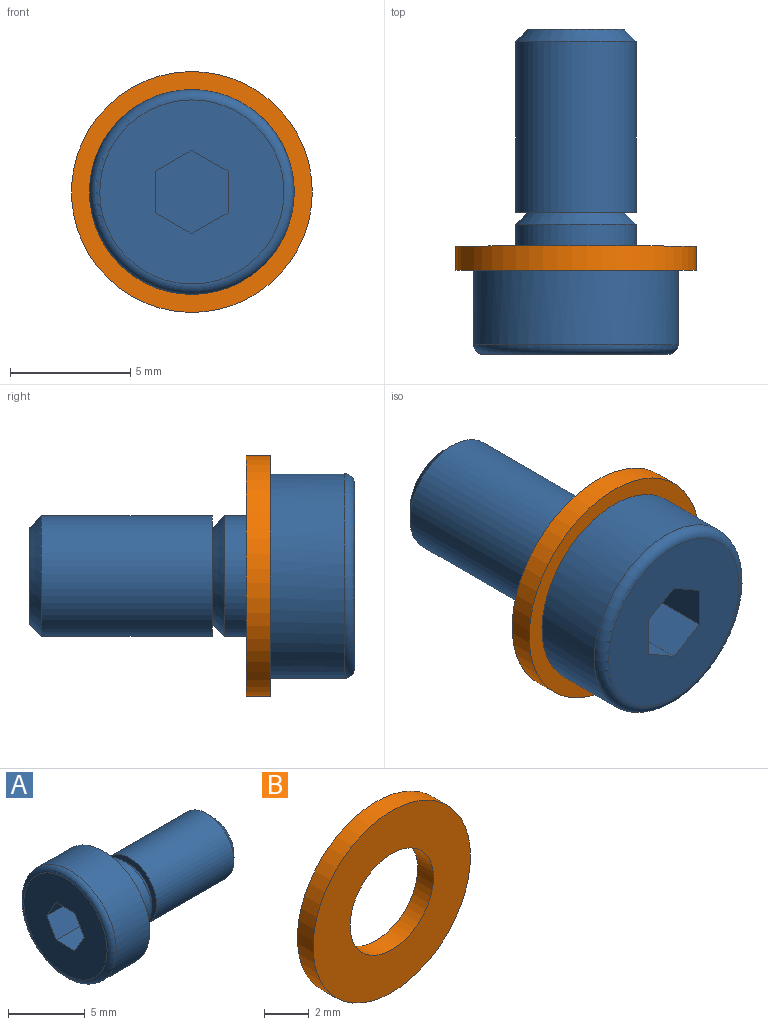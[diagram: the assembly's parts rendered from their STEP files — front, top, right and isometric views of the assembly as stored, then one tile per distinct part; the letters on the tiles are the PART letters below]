
ASSEMBLY  parts=2 mates=1
PART A: 17 faces, bbox 13.5x9.2x9.2 mm
  f0: cone r=2.25mm half-angle=45deg, axis (-1,0,0), area 10mm2, adj f1,f15
  f1: cylinder r=2.5mm len=7.1mm, axis (1,0,0), area 111.5mm2, adj f0,f14
  f2: cone r=2.25mm half-angle=45deg, axis (-1,0,0), area 10mm2, adj f3,f14
  f3: cylinder r=2.5mm len=5mm, axis (1,0,0), area 29.8mm2, adj f2,f13
  f4: cylinder r=4.25mm len=8.5mm, axis (1,0,0), area 82.1mm2, adj f5,f13
  f5: torus R=3.82mm, axis (-1,0,0), area 17.2mm2, adj f4,f16
  f6: plane 3.5x1.5mm, normal (0,0.87,-0.5), area 6.1mm2, adj f7,f11,f12,f16
  f7: plane 3.5x1.73mm, normal (0,0,-1), area 6.1mm2, adj f6,f8,f12,f16
  f8: plane 3.5x1.5mm, normal (0,-0.87,-0.5), area 6.1mm2, adj f7,f9,f12,f16
  f9: plane 3.5x1.5mm, normal (0,-0.87,0.5), area 6.1mm2, adj f8,f10,f12,f16
  f10: plane 3.5x1.73mm, normal (0,0,1), area 6.1mm2, adj f9,f11,f12,f16
  f11: plane 3.5x1.5mm, normal (0,0.87,0.5), area 6.1mm2, adj f6,f10,f12,f16
  f12: plane 3.46x3mm, normal (-1,0,0), area 7.8mm2, adj f6,f7,f8,f9,f10,f11
  f13: plane 8.5x8.5mm, normal (1,0,0), area 37.1mm2, adj f3,f4
  f14: plane 5x5mm, normal (-1,0,0), area 7.1mm2, adj f1,f2
  f15: plane 4x4mm, normal (1,0,0), area 12.6mm2, adj f0
  f16: plane 7.65x7.65mm, normal (-1,0,0), area 38.2mm2, adj f5,f6,f7,f8,f9,f10,f11
PART B: 4 faces, bbox 10x1x10 mm
  f0: cylinder r=2.65mm len=5.3mm, axis (0,1,0), area 16.7mm2, adj f2,f3
  f1: cylinder r=5mm len=10mm, axis (0,1,0), area 31.4mm2, adj f2,f3
  f2: plane 10x10mm, normal (0,1,0), area 56.5mm2, adj f0,f1
  f3: plane 10x10mm, normal (0,-1,0), area 56.5mm2, adj f0,f1
PLACE A rot(axis=(-0.58,-0.58,0.58),120deg) t=(3.49,4.25,4.11)mm
PLACE B t=(3.49,4.25,4.11)mm
MATE fastened A.f0 <-> B.f0  axis (0,1,0) through (3.49,4.25,4.11)mm
